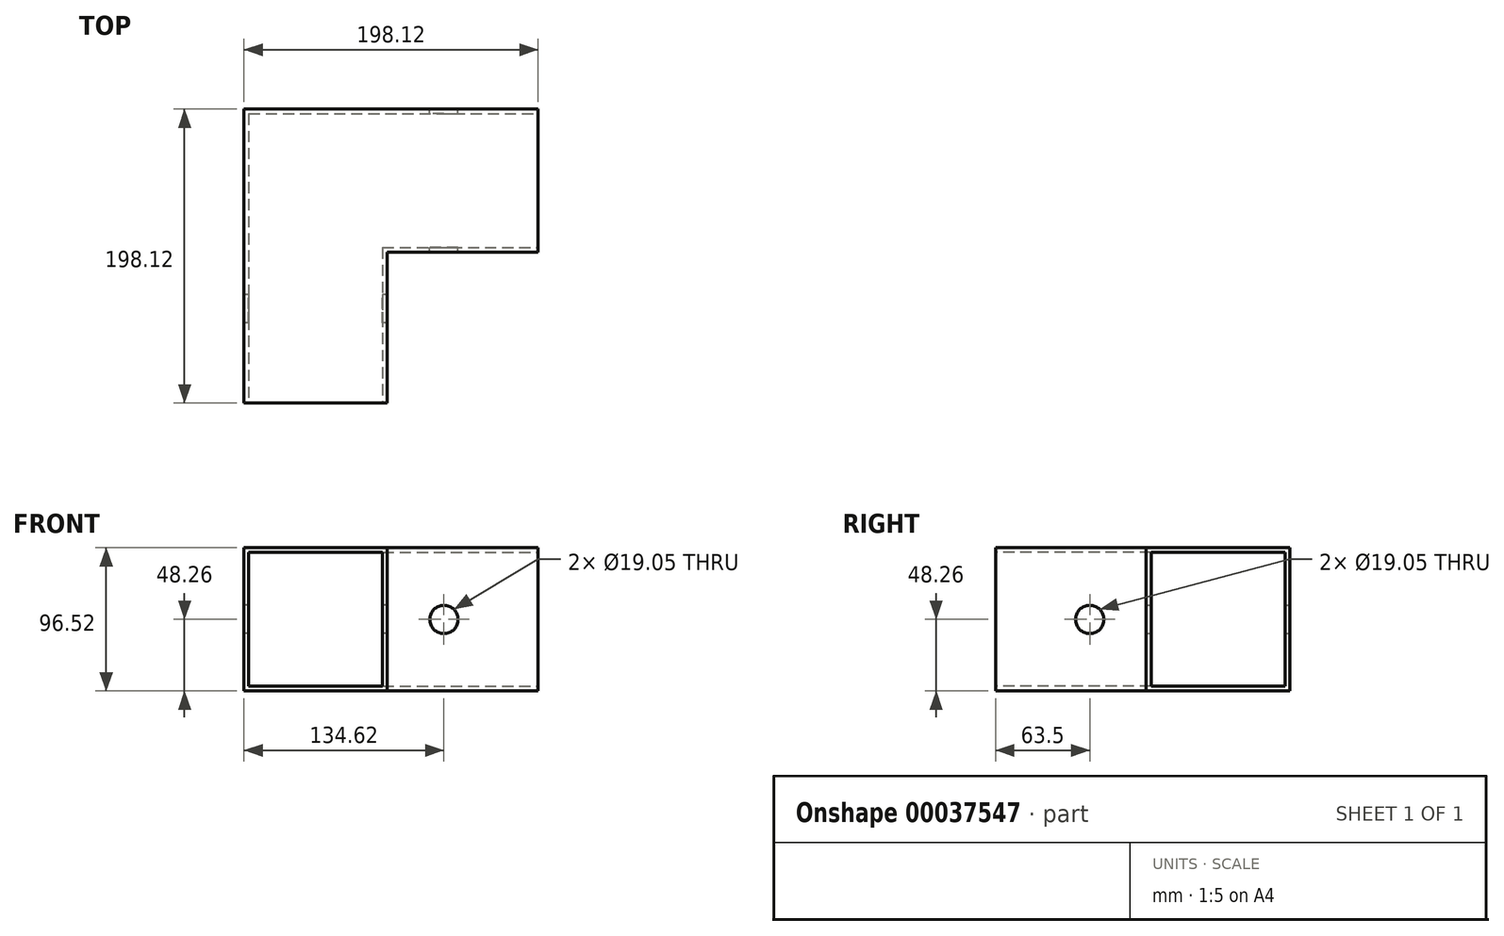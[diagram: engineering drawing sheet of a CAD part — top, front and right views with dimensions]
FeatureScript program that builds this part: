
annotation { "Feature Type Name" : "Feature", "Feature Type Description" : "" }
export const myFeature = defineFeature(function(context is Context, id is Id, definition is map)
    precondition{}
    {
        {
            var Q0;
            Q0=qCreatedBy(makeId("Top.planeOp"),FACE);
            var sketch = newSketch(context, id + "F0", { "sketchPlane" : qUnion([Q0])});
            skLineSegment(sketch, "E0", {"start": v(0, 0) * mm, "end": v(198.12, 0) * mm});
            skLineSegment(sketch, "E1", {"start": v(198.12, 0) * mm, "end": v(198.12, -96.52) * mm});
            skLineSegment(sketch, "E2", {"start": v(198.12, -96.52) * mm, "end": v(96.52, -96.52) * mm});
            skLineSegment(sketch, "E3", {"start": v(96.52, -96.52) * mm, "end": v(96.52, -198.12) * mm});
            skLineSegment(sketch, "E4", {"start": v(96.52, -198.12) * mm, "end": v(0, -198.12) * mm});
            skLineSegment(sketch, "E5", {"start": v(0, -198.12) * mm, "end": v(0, 0) * mm});
            skSolve(sketch);
        }
        {
            var Q0;
            Q0=makeQuery(id+"F0.imprint","IMPRINT",FACE,{"disambiguationData":[TD([[makeQuery(id+"F0.imprint","IMPRINT",EDGE,{"derivedFrom":sQuery(id+"F0.wireOp",EDGE,"E0")}),-1.0]])]});
            extrude(context, id + "F1", {"entities" : qUnion([Q0]), "depth" : 96.52 * mm});
        }
        {
            var Q0;
            Q0=makeQuery(id+"F1.opExtrude","SWEPT_FACE",FACE,{"disambiguationData":[OSD([sQuery(id+"F0.wireOp",EDGE,"E4")])]});
            var sketch = newSketch(context, id + "F2", { "sketchPlane" : qUnion([Q0])});
            skLineSegment(sketch, "E6.0.0", {"start": v(0, 0) * mm, "end": v(96.52, 0) * mm});
            skLineSegment(sketch, "E6.0.1", {"start": v(96.52, 0) * mm, "end": v(96.52, 96.52) * mm});
            skLineSegment(sketch, "E6.0.2", {"start": v(96.52, 96.52) * mm, "end": v(0, 96.52) * mm});
            skLineSegment(sketch, "E6.0.3", {"start": v(0, 96.52) * mm, "end": v(0, 0) * mm});
            skLineSegment(sketch, "E7.bottom", {"start": v(3.17, 93.35) * mm, "end": v(93.34, 93.35) * mm});
            skLineSegment(sketch, "E7.top", {"start": v(3.17, 3.18) * mm, "end": v(93.34, 3.18) * mm});
            skLineSegment(sketch, "E7.left", {"start": v(3.17, 93.35) * mm, "end": v(3.17, 3.18) * mm});
            skLineSegment(sketch, "E7.right", {"start": v(93.34, 93.35) * mm, "end": v(93.34, 3.18) * mm});
            skSolve(sketch);
        }
        {
            var Q0;
            Q0=makeQuery(id+"F2.imprint","IMPRINT",FACE,{"disambiguationData":[TD([[makeQuery(id+"F2.imprint","IMPRINT",EDGE,{"derivedFrom":sQuery(id+"F2.wireOp",EDGE,"E7.bottom")}),-1.0]])]});
            var Q1;
            Q1=makeQuery(id+"F1.opExtrude","SWEPT_FACE",FACE,{"disambiguationData":[OSD([sQuery(id+"F0.wireOp",EDGE,"E2")])]});
            extrude(context, id + "F3", {"entities" : qUnion([Q0]), "operationType" : NewBodyOperationType.REMOVE, "oppositeDirection" : true, "endBoundEntityFace" : qUnion([Q1]), "depth" : 106.68 * mm});
        }
        {
            var Q0;
            Q0=makeQuery(id+"F1.opExtrude","SWEPT_FACE",FACE,{"disambiguationData":[OSD([sQuery(id+"F0.wireOp",EDGE,"E1")])]});
            var sketch = newSketch(context, id + "F4", { "sketchPlane" : qUnion([Q0])});
            skLineSegment(sketch, "E8.0.0", {"start": v(-96.52, 0) * mm, "end": v(0, 0) * mm});
            skLineSegment(sketch, "E8.0.1", {"start": v(0, 0) * mm, "end": v(0, 96.52) * mm});
            skLineSegment(sketch, "E8.0.2", {"start": v(0, 96.52) * mm, "end": v(-96.52, 96.52) * mm});
            skLineSegment(sketch, "E8.0.3", {"start": v(-96.52, 96.52) * mm, "end": v(-96.52, 0) * mm});
            skLineSegment(sketch, "E9.bottom", {"start": v(-93.35, 93.34) * mm, "end": v(-3.18, 93.35) * mm});
            skLineSegment(sketch, "E9.top", {"start": v(-93.35, 3.17) * mm, "end": v(-3.18, 3.18) * mm});
            skLineSegment(sketch, "E9.left", {"start": v(-93.35, 93.34) * mm, "end": v(-93.35, 3.17) * mm});
            skLineSegment(sketch, "E9.right", {"start": v(-3.18, 93.35) * mm, "end": v(-3.18, 3.18) * mm});
            skSolve(sketch);
        }
        {
            var Q0;
            Q0=makeQuery(id+"F4.imprint","IMPRINT",FACE,{"disambiguationData":[TD([[makeQuery(id+"F4.imprint","IMPRINT",EDGE,{"derivedFrom":sQuery(id+"F4.wireOp",EDGE,"E9.bottom")}),-1.0]])]});
            var Q1;
            Q1=makeQuery(id+"F3.boolean.opBoolean","COPY",FACE,{"derivedFrom":makeQuery(id+"F3.opExtrude","SWEPT_FACE",FACE,{"disambiguationData":[OSD([sQuery(id+"F2.wireOp",EDGE,"E7.left")])]})});
            extrude(context, id + "F5", {"entities" : qUnion([Q0]), "operationType" : NewBodyOperationType.REMOVE, "endBound" : BoundingType.UP_TO_SURFACE, "oppositeDirection" : true, "endBoundEntityFace" : qUnion([Q1]), "depth" : 25.4 * mm});
        }
        {
            var Q0;
            Q0=makeQuery(id+"F1.opExtrude","SWEPT_FACE",FACE,{"disambiguationData":[OSD([sQuery(id+"F0.wireOp",EDGE,"E5")])]});
            var sketch = newSketch(context, id + "F6", { "sketchPlane" : qUnion([Q0])});
            skPoint(sketch, "E10", {"position": v(134.62, 48.26) * mm});
            skLineSegment(sketch, "E11.0", {"start": v(198.12, 96.52) * mm, "end": v(198.12, 0) * mm});
            skLineSegment(sketch, "E12", {"start": v(134.62, 48.26) * mm, "end": v(198.12, 48.26) * mm, "construction": true});
            skSolve(sketch);
        }
        {
            var Q0;
            Q0=makeQuery(id+"F1.opExtrude","SWEPT_FACE",FACE,{"disambiguationData":[OSD([sQuery(id+"F0.wireOp",EDGE,"E0")])]});
            var sketch = newSketch(context, id + "F7", { "sketchPlane" : qUnion([Q0])});
            skPoint(sketch, "E13", {"position": v(-134.62, 48.26) * mm});
            skLineSegment(sketch, "E14.0", {"start": v(-198.12, 96.52) * mm, "end": v(-198.12, 0) * mm});
            skLineSegment(sketch, "E15.0", {"start": v(0, 96.52) * mm, "end": v(-198.12, 96.52) * mm});
            skLineSegment(sketch, "E16.0.0", {"start": v(-198.12, 0) * mm, "end": v(0, 0) * mm});
            skLineSegment(sketch, "E16.0.1", {"start": v(0, 0) * mm, "end": v(0, 96.52) * mm});
            skLineSegment(sketch, "E17", {"start": v(-198.12, 48.26) * mm, "end": v(-134.62, 48.26) * mm, "construction": true});
            skSolve(sketch);
        }
        {
            var Q0;
            Q0=sQuery(id+"F7.wireOp",VERTEX,"E13");
            var Q1;
            Q1=sQuery(id+"F6.wireOp",VERTEX,"E10");
            var Q2;
            Q2=makeQuery(id+"F1.opExtrude","SWEPT_BODY",BODY,{"disambiguationData":[OSD([sQuery(id+"F0.wireOp",EDGE,"E0"),sQuery(id+"F0.wireOp",EDGE,"E1"),sQuery(id+"F0.wireOp",EDGE,"E2"),sQuery(id+"F0.wireOp",EDGE,"E3"),sQuery(id+"F0.wireOp",EDGE,"E4"),sQuery(id+"F0.wireOp",EDGE,"E5")])]});
            hole(context, id + "F8", {"style" : HoleStyle.SIMPLE, "holeDiameter" : 19.05 * mm, "endStyle" : HoleEndStyle.THROUGH, "locations" : qUnion([Q0, Q1]), "scope" : qUnion([Q2])});
        }
    });
